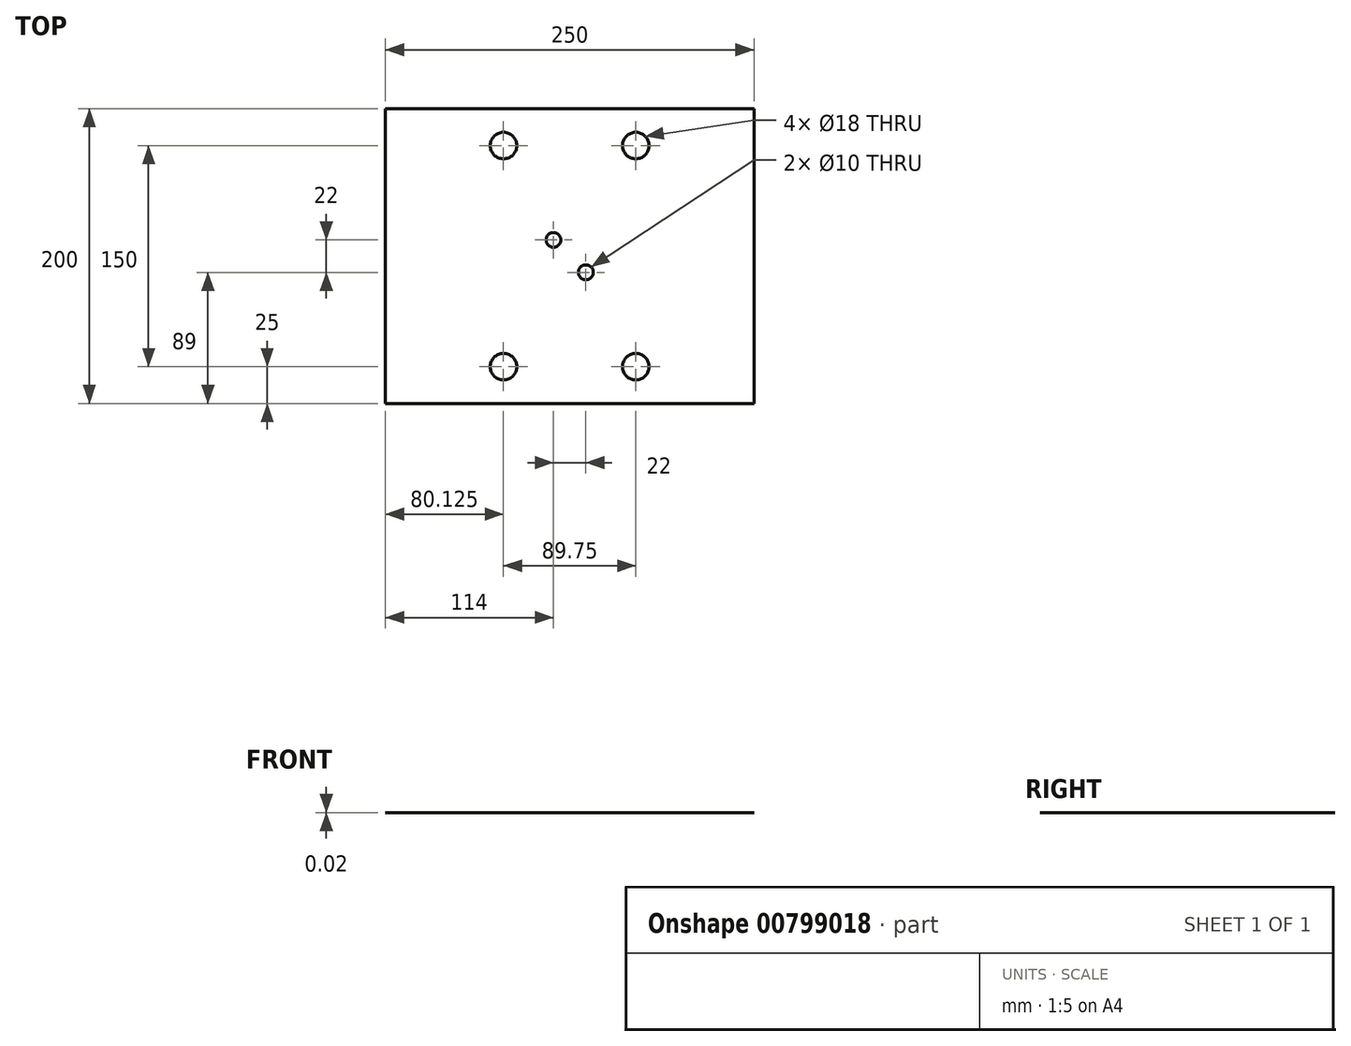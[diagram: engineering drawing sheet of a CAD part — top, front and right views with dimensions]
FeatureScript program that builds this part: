
annotation { "Feature Type Name" : "Feature", "Feature Type Description" : "" }
export const myFeature = defineFeature(function(context is Context, id is Id, definition is map)
    precondition{}
    {
        {
            var Q0;
            Q0=qCreatedBy(makeId("Top.planeOp"),FACE);
            var sketch = newSketch(context, id + "F0", { "sketchPlane" : qUnion([Q0])});
            skLineSegment(sketch, "E0.bottom", {"start": v(-125, -100) * mm, "end": v(125, -100) * mm});
            skLineSegment(sketch, "E0.top", {"start": v(-125, 100) * mm, "end": v(125, 100) * mm});
            skLineSegment(sketch, "E0.left", {"start": v(-125, -100) * mm, "end": v(-125, 100) * mm});
            skLineSegment(sketch, "E0.right", {"start": v(125, -100) * mm, "end": v(125, 100) * mm});
            skPoint(sketch, "E0.middle", {"position": v(0, 0) * mm});
            skCircle(sketch, "E1", {"center": v(-44.88, -75) * mm, "radius": 3.56 * mm});
            skCircle(sketch, "E2", {"center": v(-11, 11) * mm, "radius": 2.5 * mm});
            skCircle(sketch, "E3", {"center": v(-44.88, 75) * mm, "radius": 3.56 * mm});
            skCircle(sketch, "E4", {"center": v(11, -11) * mm, "radius": 2.5 * mm});
            skCircle(sketch, "E5", {"center": v(44.88, -75) * mm, "radius": 2.5 * mm});
            skCircle(sketch, "E6", {"center": v(44.88, 75) * mm, "radius": 2.5 * mm});
            skLineSegment(sketch, "E7", {"start": v(-44.88, 75) * mm, "end": v(-44.88, -75) * mm, "construction": true});
            skLineSegment(sketch, "E8", {"start": v(44.88, 75) * mm, "end": v(44.88, -75) * mm, "construction": true});
            skLineSegment(sketch, "E9", {"start": v(-44.88, 75) * mm, "end": v(44.88, 75) * mm, "construction": true});
            skLineSegment(sketch, "E10", {"start": v(-44.88, -75) * mm, "end": v(44.88, -75) * mm, "construction": true});
            skSolve(sketch);
        }
        {
            var Q0;
            Q0=qSketchRegion(id+"F0",true);
            extrude(context, id + "F1", {"entities" : qUnion([Q0]), "depth" : 1 / 50.8 * mm, "offsetDistance" : 25 * mm});
        }
        {
            var Q0;
            Q0=makeQuery(id+"F1.opExtrude","CAP_FACE",FACE,{"disambiguationData":[OSD([sQuery(id+"F0.wireOp",EDGE,"E0.bottom"),sQuery(id+"F0.wireOp",EDGE,"E0.top"),sQuery(id+"F0.wireOp",EDGE,"E0.left"),sQuery(id+"F0.wireOp",EDGE,"E0.right"),sQuery(id+"F0.wireOp",EDGE,"E1"),sQuery(id+"F0.wireOp",EDGE,"E2"),sQuery(id+"F0.wireOp",EDGE,"E3"),sQuery(id+"F0.wireOp",EDGE,"E4"),sQuery(id+"F0.wireOp",EDGE,"E5"),sQuery(id+"F0.wireOp",EDGE,"E6")])],"isStart":false});
            var sketch = newSketch(context, id + "F2", { "sketchPlane" : qUnion([Q0])});
            skCircle(sketch, "E11", {"center": v(-44.88, 75) * mm, "radius": 9 * mm});
            skCircle(sketch, "E12", {"center": v(44.88, 75) * mm, "radius": 9 * mm});
            skCircle(sketch, "E13", {"center": v(-44.88, -75) * mm, "radius": 9 * mm});
            skCircle(sketch, "E14", {"center": v(44.88, -75) * mm, "radius": 9 * mm});
            skCircle(sketch, "E15", {"center": v(-11, 11) * mm, "radius": 5 * mm});
            skCircle(sketch, "E16", {"center": v(11, -11) * mm, "radius": 5 * mm});
            skSolve(sketch);
        }
        {
            var Q0;
            Q0=qSketchRegion(id+"F2",true);
            extrude(context, id + "F3", {"entities" : qUnion([Q0]), "operationType" : NewBodyOperationType.REMOVE, "oppositeDirection" : true, "depth" : 6 * mm, "offsetDistance" : 25 * mm});
        }
    });
